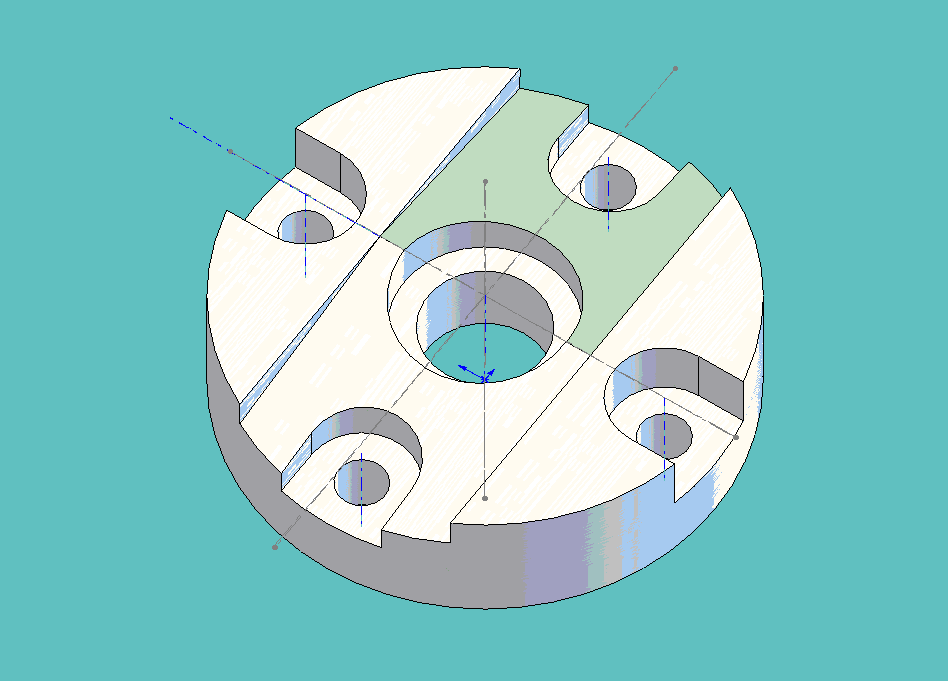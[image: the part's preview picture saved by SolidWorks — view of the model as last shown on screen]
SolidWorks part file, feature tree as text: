
SOLIDWORKS PART (.sldprt)
format: sldprt  version: not decoded by parser v0  size: 395,264 bytes
history: native  units: mm
features: sketch x9, cut_extrude x4, plane x3, material x1, extrude x1, cut_revolve x1, mirror x1, pattern_circular x1 (+10 scaffold rows collapsed)
feature tree (31):
  scaffold x10  (default folders/planes/origin — collapsed)
  material  "Nickel"
  plane  "Frontal"
  plane  "Horizontal"
  plane  "Profile"
  sketch  "Sketch1"  dims[D1=110.744mm]
  extrude  "Extrude1"  Depth=29.464mm
  sketch  "Sketch2"
  sketch  "Sketch3"
  sketch  "Sketch4"  dims[D3=27.432mm D1=25.4mm D2=25.4mm]
  cut_extrude  "Cut-Extrude1"  Depth=29.464mm
  sketch  "Sketch5"  dims[D1=39.116mm]
  cut_extrude  "Cut-Extrude2"  Depth=11.176mm
  sketch  "Sketch6"  dims[D1=50.8mm D2=25.4mm]
  cut_revolve  "Cut-Revolve1"  Angle=8deg
  mirror  "Mirror1"
  sketch  "Sketch9"  dims[c1.D1=~37.946082mm c1.D3=~44.753972mm c2.D1=24.13mm c2.D2=12.065mm c2.D3=~22.369394mm c3.D1=24.13mm c3.D2=12.065mm]
  cut_extrude  "Cut-Extrude4"  [1 undecoded]
  sketch  "Sketch12"  dims[D1=~4.84224mm]
  cut_extrude  "Cut-Extrude5"  [1 undecoded]
  sketch  "Sketch17"
  pattern_circular  "CirPattern1"  Count=4  [1 undecoded]
decode coverage: 11 of 17 modeling features carry decoded parameters
note: ~ marks probable driven/reference dimensions
note: 3 parameter values undecoded
note: suppression state not decoded; provenance and decode notes live in map.json
